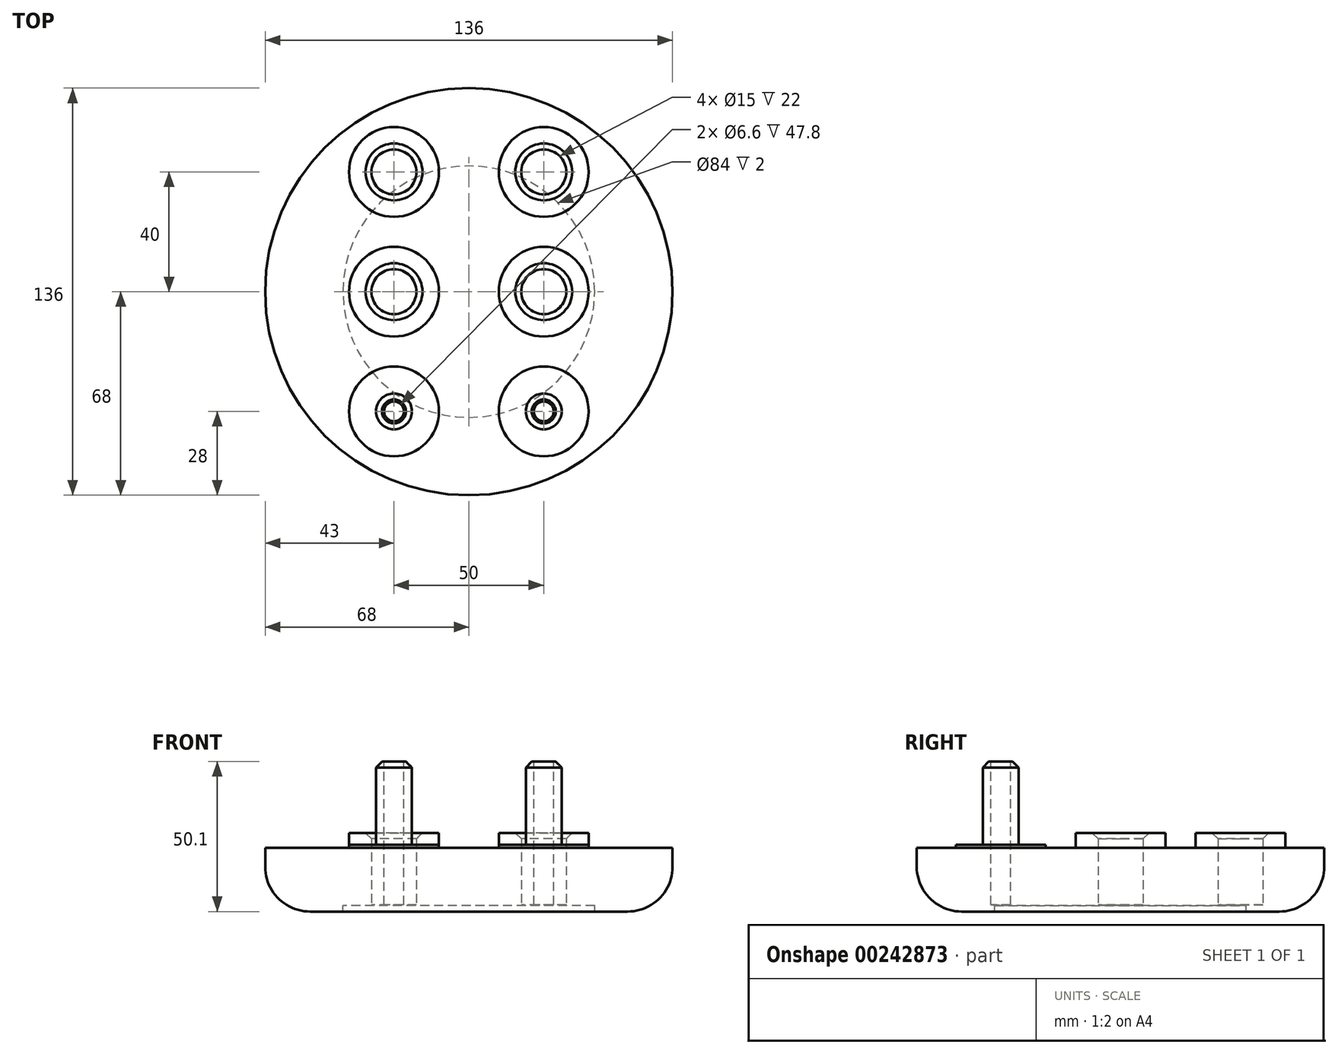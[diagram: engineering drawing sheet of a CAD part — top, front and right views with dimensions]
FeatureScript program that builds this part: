
annotation { "Feature Type Name" : "Feature", "Feature Type Description" : "" }
export const myFeature = defineFeature(function(context is Context, id is Id, definition is map)
    precondition{}
    {
        {
            var Q0;
            Q0=qCreatedBy(makeId("Front.planeOp"),FACE);
            var sketch = newSketch(context, id + "F0", { "sketchPlane" : qUnion([Q0])});
            skLineSegment(sketch, "E0.bottom", {"start": v(0, 0) * mm, "end": v(-68, 0) * mm});
            skLineSegment(sketch, "E0.top", {"start": v(-42, -21.3) * mm, "end": v(-53, -21.3) * mm});
            skLineSegment(sketch, "E0.left", {"start": v(0, 0) * mm, "end": v(0, -19.3) * mm});
            skLineSegment(sketch, "E0.right", {"start": v(-68, 0) * mm, "end": v(-68, -6.3) * mm});
            skLineSegment(sketch, "E1.top", {"start": v(0, -19.3) * mm, "end": v(-42, -19.3) * mm});
            skLineSegment(sketch, "E1.right", {"start": v(-42, -21.3) * mm, "end": v(-42, -19.3) * mm});
            skPoint(sketch, "E2.visualSharp", {"position": v(-68, -21.3) * mm});
            skArc(sketch, "E2.filletArc", {"start": v(-68, -6.3) * mm, "mid": v(-63.6, -16.9) * mm, "end": v(-53, -21.3) * mm});
            skSolve(sketch);
        }
        {
            var Q0;
            Q0=makeQuery(id+"F0.imprint","IMPRINT",FACE,{"disambiguationData":[TD([[makeQuery(id+"F0.imprint","IMPRINT",EDGE,{"derivedFrom":sQuery(id+"F0.wireOp",EDGE,"E0.bottom")}),1.0]])]});
            var Q1;
            Q1=sQuery(id+"F0.wireOp",EDGE,"E0.left");
            revolve(context, id + "F1", {"entities" : qUnion([Q0]), "axis" : qUnion([Q1]), "revolveType" : RevolveType.FULL});
        }
        {
            var Q0;
            Q0=makeQuery(id+"F1.opRevolve","SWEPT_FACE",FACE,{"disambiguationData":[OSD([sQuery(id+"F0.wireOp",EDGE,"E0.bottom")])]});
            var sketch = newSketch(context, id + "F2", { "sketchPlane" : qUnion([Q0])});
            skLineSegment(sketch, "E3.bottom", {"start": v(0, 0) * mm, "end": v(25, 0) * mm, "construction": true});
            skLineSegment(sketch, "E3.top", {"start": v(0, 40) * mm, "end": v(25, 40) * mm, "construction": true});
            skLineSegment(sketch, "E3.left", {"start": v(0, 0) * mm, "end": v(0, 40) * mm, "construction": true});
            skLineSegment(sketch, "E3.right", {"start": v(25, 0) * mm, "end": v(25, 40) * mm, "construction": true});
            skLineSegment(sketch, "E4.bottom", {"start": v(0, 0) * mm, "end": v(-25, 0) * mm, "construction": true});
            skLineSegment(sketch, "E4.top", {"start": v(0, 40) * mm, "end": v(-25, 40) * mm, "construction": true});
            skLineSegment(sketch, "E4.right", {"start": v(-25, 0) * mm, "end": v(-25, 40) * mm, "construction": true});
            skLineSegment(sketch, "E5.bottom", {"start": v(25, 0) * mm, "end": v(-25, 0) * mm, "construction": true});
            skLineSegment(sketch, "E5.top", {"start": v(25, -40) * mm, "end": v(-25, -40) * mm, "construction": true});
            skLineSegment(sketch, "E5.left", {"start": v(25, 0) * mm, "end": v(25, -40) * mm, "construction": true});
            skLineSegment(sketch, "E5.right", {"start": v(-25, 0) * mm, "end": v(-25, -40) * mm, "construction": true});
            skCircle(sketch, "E6", {"center": v(25, 40) * mm, "radius": 15 * mm});
            skCircle(sketch, "E7", {"center": v(-25, 40) * mm, "radius": 15 * mm});
            skCircle(sketch, "E8", {"center": v(25, 0) * mm, "radius": 15 * mm});
            skCircle(sketch, "E9", {"center": v(-25, 0) * mm, "radius": 15 * mm});
            skCircle(sketch, "E10", {"center": v(25, 40) * mm, "radius": 7.5 * mm});
            skCircle(sketch, "E11", {"center": v(-25, 40) * mm, "radius": 7.5 * mm});
            skCircle(sketch, "E12", {"center": v(-25, 0) * mm, "radius": 7.5 * mm});
            skCircle(sketch, "E13", {"center": v(25, 0) * mm, "radius": 7.5 * mm});
            skCircle(sketch, "E14", {"center": v(25, -40) * mm, "radius": 6 * mm});
            skCircle(sketch, "E15", {"center": v(-25, -40) * mm, "radius": 6 * mm});
            skCircle(sketch, "E16", {"center": v(-25, -40) * mm, "radius": 3.3 * mm});
            skCircle(sketch, "E17", {"center": v(25, -40) * mm, "radius": 3.3 * mm});
            skCircle(sketch, "E18", {"center": v(-25, -40) * mm, "radius": 15 * mm});
            skCircle(sketch, "E19", {"center": v(25, -40) * mm, "radius": 15 * mm});
            skSolve(sketch);
        }
        {
            var Q0;
            Q0=makeQuery(id+"F2.imprint","IMPRINT",FACE,{"disambiguationData":[TD([[makeQuery(id+"F2.imprint","IMPRINT",EDGE,{"derivedFrom":sQuery(id+"F2.wireOp",EDGE,"E7")}),1.0]])]});
            var Q1;
            Q1=makeQuery(id+"F2.imprint","IMPRINT",FACE,{"disambiguationData":[TD([[makeQuery(id+"F2.imprint","IMPRINT",EDGE,{"derivedFrom":sQuery(id+"F2.wireOp",EDGE,"E6")}),1.0]])]});
            var Q2;
            Q2=makeQuery(id+"F2.imprint","IMPRINT",FACE,{"disambiguationData":[TD([[makeQuery(id+"F2.imprint","IMPRINT",EDGE,{"derivedFrom":sQuery(id+"F2.wireOp",EDGE,"E8")}),1.0]])]});
            var Q3;
            Q3=makeQuery(id+"F2.imprint","IMPRINT",FACE,{"disambiguationData":[TD([[makeQuery(id+"F2.imprint","IMPRINT",EDGE,{"derivedFrom":sQuery(id+"F2.wireOp",EDGE,"E9")}),1.0]])]});
            extrude(context, id + "F3", {"entities" : qUnion([Q0, Q1, Q2, Q3]), "operationType" : NewBodyOperationType.ADD, "depth" : 5 * mm});
        }
        {
            var Q0;
            Q0=makeQuery(id+"F2.imprint","IMPRINT",FACE,{"disambiguationData":[TD([[makeQuery(id+"F2.imprint","IMPRINT",EDGE,{"derivedFrom":sQuery(id+"F2.wireOp",EDGE,"E11")}),1.0]])]});
            var Q1;
            Q1=makeQuery(id+"F2.imprint","IMPRINT",FACE,{"disambiguationData":[TD([[makeQuery(id+"F2.imprint","IMPRINT",EDGE,{"derivedFrom":sQuery(id+"F2.wireOp",EDGE,"E10")}),1.0]])]});
            var Q2;
            Q2=makeQuery(id+"F2.imprint","IMPRINT",FACE,{"disambiguationData":[TD([[makeQuery(id+"F2.imprint","IMPRINT",EDGE,{"derivedFrom":sQuery(id+"F2.wireOp",EDGE,"E13")}),1.0]])]});
            var Q3;
            Q3=makeQuery(id+"F2.imprint","IMPRINT",FACE,{"disambiguationData":[TD([[makeQuery(id+"F2.imprint","IMPRINT",EDGE,{"derivedFrom":sQuery(id+"F2.wireOp",EDGE,"E12")}),1.0]])]});
            var Q4;
            Q4=makeQuery(id+"F2.imprint","IMPRINT",FACE,{"disambiguationData":[TD([[makeQuery(id+"F2.imprint","IMPRINT",EDGE,{"derivedFrom":sQuery(id+"F2.wireOp",EDGE,"E16")}),1.0]])]});
            var Q5;
            Q5=makeQuery(id+"F2.imprint","IMPRINT",FACE,{"disambiguationData":[TD([[makeQuery(id+"F2.imprint","IMPRINT",EDGE,{"derivedFrom":sQuery(id+"F2.wireOp",EDGE,"E17")}),1.0]])]});
            extrude(context, id + "F4", {"entities" : qUnion([Q0, Q1, Q2, Q3, Q4, Q5]), "operationType" : NewBodyOperationType.REMOVE, "oppositeDirection" : true, "depth" : 19 * mm});
        }
        {
            var Q0;
            Q0=makeQuery(id+"F2.imprint","IMPRINT",FACE,{"disambiguationData":[TD([[makeQuery(id+"F2.imprint","IMPRINT",EDGE,{"derivedFrom":sQuery(id+"F2.wireOp",EDGE,"E15")}),1.0]])]});
            var Q1;
            Q1=makeQuery(id+"F2.imprint","IMPRINT",FACE,{"disambiguationData":[TD([[makeQuery(id+"F2.imprint","IMPRINT",EDGE,{"derivedFrom":sQuery(id+"F2.wireOp",EDGE,"E14")}),1.0]])]});
            extrude(context, id + "F5", {"entities" : qUnion([Q0, Q1]), "operationType" : NewBodyOperationType.ADD, "depth" : 28.8 * mm});
        }
        {
            var Q0;
            Q0=makeQuery(id+"F2.imprint","IMPRINT",FACE,{"disambiguationData":[TD([[makeQuery(id+"F2.imprint","IMPRINT",EDGE,{"derivedFrom":sQuery(id+"F2.wireOp",EDGE,"E15")}),-1.0]])]});
            var Q1;
            Q1=makeQuery(id+"F2.imprint","IMPRINT",FACE,{"disambiguationData":[TD([[makeQuery(id+"F2.imprint","IMPRINT",EDGE,{"derivedFrom":sQuery(id+"F2.wireOp",EDGE,"E14")}),-1.0]])]});
            extrude(context, id + "F6", {"entities" : qUnion([Q0, Q1]), "operationType" : NewBodyOperationType.ADD, "depth" : 1 * mm});
        }
        {
            var Q0;
            Q0=makeQuery(id+"F3.opExtrude","CAP_EDGE",EDGE,{"disambiguationData":[OSD([sQuery(id+"F2.wireOp",EDGE,"E11")])],"isStart":false});
            var Q1;
            Q1=makeQuery(id+"F3.opExtrude","CAP_EDGE",EDGE,{"disambiguationData":[OSD([sQuery(id+"F2.wireOp",EDGE,"E10")])],"isStart":false});
            var Q2;
            Q2=makeQuery(id+"F3.opExtrude","CAP_EDGE",EDGE,{"disambiguationData":[OSD([sQuery(id+"F2.wireOp",EDGE,"E13")])],"isStart":false});
            var Q3;
            Q3=makeQuery(id+"F3.opExtrude","CAP_EDGE",EDGE,{"disambiguationData":[OSD([sQuery(id+"F2.wireOp",EDGE,"E12")])],"isStart":false});
            var Q4;
            Q4=makeQuery(id+"F5.opExtrude","CAP_EDGE",EDGE,{"disambiguationData":[OSD([sQuery(id+"F2.wireOp",EDGE,"E15")])],"isStart":false});
            var Q5;
            Q5=makeQuery(id+"F5.opExtrude","CAP_EDGE",EDGE,{"disambiguationData":[OSD([sQuery(id+"F2.wireOp",EDGE,"E14")])],"isStart":false});
            chamfer(context, id + "F7", {"entities" : qUnion([Q0, Q1, Q2, Q3, Q4, Q5]), "width" : 2 * mm, "tangentPropagation" : true});
        }
    });
